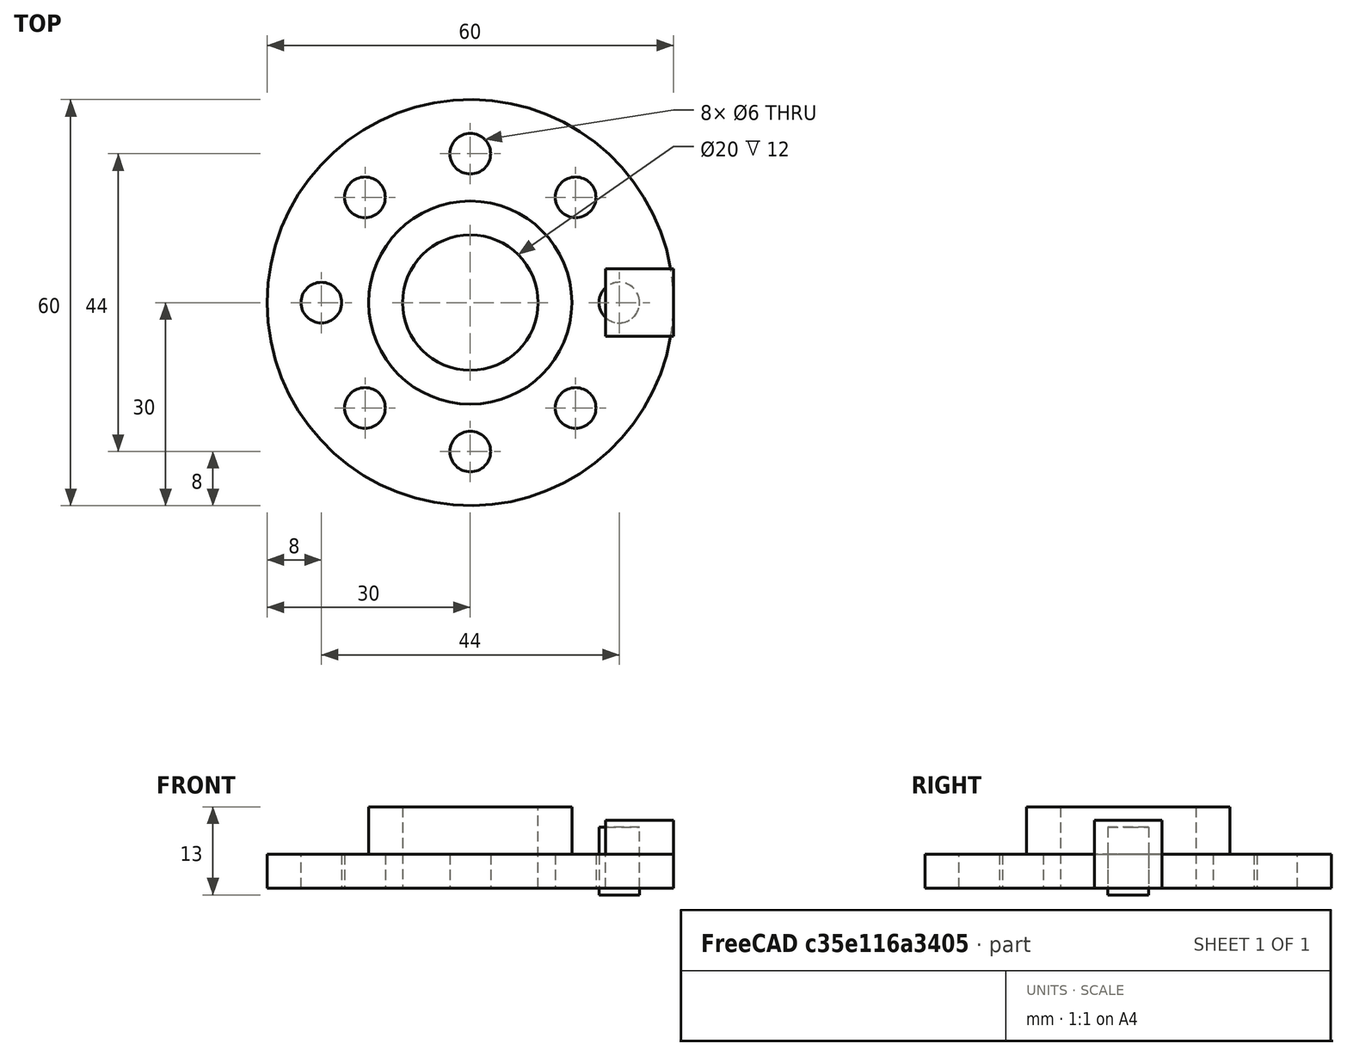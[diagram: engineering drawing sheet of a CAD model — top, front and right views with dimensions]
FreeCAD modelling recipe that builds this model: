
FCSTD DOCUMENT  (FreeCAD 1.0R39319 (Git))
Label: ojt1_t11p01_flange
License: All rights reserved
LicenseURL: https://en.wikipedia.org/wiki/All_rights_reserved
objects: Part::Cylinder×4, Part::FeaturePython×2, Part::Cut×2, Part::Box×1, Part::MultiFuse×1
note: 8 computed .brp shape members not serialized (recipe doc carries the construction recipe); baked Part::Feature solids carry a one-line shape summary decoded from their .brp

FEATURE [Part::Box] Box  label="Cub"
  AttacherType = Attacher::AttachEngine3D
  Height = 10
  Length = 10
  Placement = pos=(20,-5,0) rot=(0,0,1;0rad)
  Width = 10
FEATURE [Part::FeaturePython] Array  # Draft array (typed FeaturePython)
  AlwaysSyncPlacement = false
  Angle = 180
  ArrayType = 1
  Axis = (0,0,1)
  Base = -> Box
  Center = (0,0,0)
  Count = 6
  ExpandArray = false
  Fuse = false
  IntervalAxis = (0,0,1)
  IntervalX = (100,0,0)
  IntervalY = (0,100,0)
  IntervalZ = (0,0,100)
  NumberCircles = 3
  NumberPolar = 6
  NumberX = 2
  NumberY = 2
  NumberZ = 1
  PlacementList = 6 placements: [(20,-5,0),(19.1193,7.71062,1),(10.9356,17.476,2),(-1.42506,20.5662,3),(-13.2414,15.8008,4),(-20,5,5)]
  RadialDistance = 50
  ScaleList = (6) [(1,1,1),(1,1,1),(1,1,1),(1,1,1),(1,1,1),(1,1,1)]
  Symmetry = 1
  TangentialDistance = 25
FEATURE [Part::Cylinder] Cylinder  label="base"
  Angle = 360
  AttacherType = Attacher::AttachEngine3D
  FirstAngle = 0
  Height = 5
  Radius = 30
  SecondAngle = 0
FEATURE [Part::Cylinder] Cylinder001  label="tub exterior"
  Angle = 360
  AttacherType = Attacher::AttachEngine3D
  FirstAngle = 0
  Height = 12
  Radius = 15
  SecondAngle = 0
FEATURE [Part::MultiFuse] Fusion  label="brida sin taladros"
  Refine = true
  Shapes = -> [Cylinder,Cylinder001]
FEATURE [Part::Cylinder] Cylinder002  label="brida sin taladros001"
  Angle = 360
  AttacherType = Attacher::AttachEngine3D
  FirstAngle = 0
  Height = 30
  Placement = pos=(0,0,-1) rot=(0,0,1;0rad)
  Radius = 10
  SecondAngle = 0
FEATURE [Part::Cut] Cut
  Base = -> Fusion
  Refine = true
  Tool = -> Cylinder002
FEATURE [Part::Cylinder] Cylinder003  label="taladro master"
  Angle = 360
  AttacherType = Attacher::AttachEngine3D
  FirstAngle = 0
  Height = 10
  Placement = pos=(22,0,-1) rot=(0,0,1;0rad)
  Radius = 3
  SecondAngle = 0
FEATURE [Part::FeaturePython] Array001  # Draft array (typed FeaturePython)
  AlwaysSyncPlacement = false
  Angle = 360
  ArrayType = 1
  Axis = (0,0,1)
  Base = -> Cylinder003
  Center = (0,0,0)
  Count = 8
  ExpandArray = false
  Fuse = false
  IntervalAxis = (0,0,0)
  IntervalX = (100,0,0)
  IntervalY = (0,100,0)
  IntervalZ = (0,0,100)
  NumberCircles = 3
  NumberPolar = 8
  NumberX = 2
  NumberY = 2
  NumberZ = 1
  PlacementList = 8 placements: [(22,0,-1),(15.5563,15.5563,-1),(0,22,-1),(-15.5563,15.5563,-1),(-22,2.69422e-15,-1),(-15.5563,-15.5563,-1),(-4.88498e-15,-22,-1),(15.5563,-15.5563,-1)]
  RadialDistance = 50
  ScaleList = (8) [(1,1,1),(1,1,1),(1,1,1),(1,1,1),(1,1,1),(1,1,1),(1,1,1),(1,1,1)]
  Symmetry = 1
  TangentialDistance = 25
FEATURE [Part::Cut] Cut001
  Base = -> Cut
  Refine = true
  Tool = -> Array001
